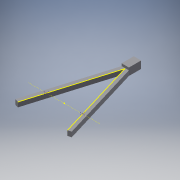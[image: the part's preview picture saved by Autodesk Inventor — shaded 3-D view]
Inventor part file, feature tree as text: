
AUTODESK INVENTOR PART (.ipt)
format: ipt  version: 2018 (Build 220112000, 112)  size: 131,584 bytes
history: native  units: mm
features: sketch x3, extrude x2
ambient origin geometry x8: Origin, YZ Plane, XZ Plane, XY Plane, X Axis, Y Axis, Z Axis, Center Point
bodies: Volumenkörper1 (feature_tree)
feature tree (5):
  extrude  "Extrusion1"  Depth=75.0mm
  extrude  "Extrusion2"  Depth=25.0mm
  sketch  "Skizze3"  dims[d4=15.0mm d5=90.0mm d6=175.0mm d7=175.0mm d8=7.5mm d9=7.5mm d10=10.0mm d11=0.0mm d12=5.0mm d13=0.0mm]
  sketch  "Skizze1"  dims[d0=150.0mm d1=75.0mm]
  sketch  "Skizze2"  dims[d2=125.0mm d3=25.0mm]
